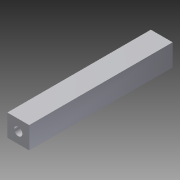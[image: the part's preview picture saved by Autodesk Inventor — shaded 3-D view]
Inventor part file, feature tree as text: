
AUTODESK INVENTOR PART (.ipt)
format: ipt  version: 2015 (Build 190159000, 159)  size: 80,896 bytes
history: native  units: mm
features: sketch x2, extrude x1, hole x1
ambient origin geometry x8: Origin, YZ Plane, XZ Plane, XY Plane, X Axis, Y Axis, Z Axis, Center Point
bodies: Solid1 (feature_tree)
feature tree (4):
  extrude  "Extrusion1"  Depth=7.0mm
  hole  "Hole1"  [1 undecoded]
  sketch  "Sketch1"  dims[d0=7.0mm d1=7.0mm]
  sketch  "Sketch2"  dims[d2=46.0mm d3=0.0mm d4=2.616mm d5=6.0mm d6=4.0mm d7=2.0mm d8=90.0deg d9=5.0mm d10=0.0mm]
note: 1 required parameter value undecoded (feature->parameter linkage not recoverable at this tier; creation-order binding heuristic only, values carry confidence <= 0.55)
